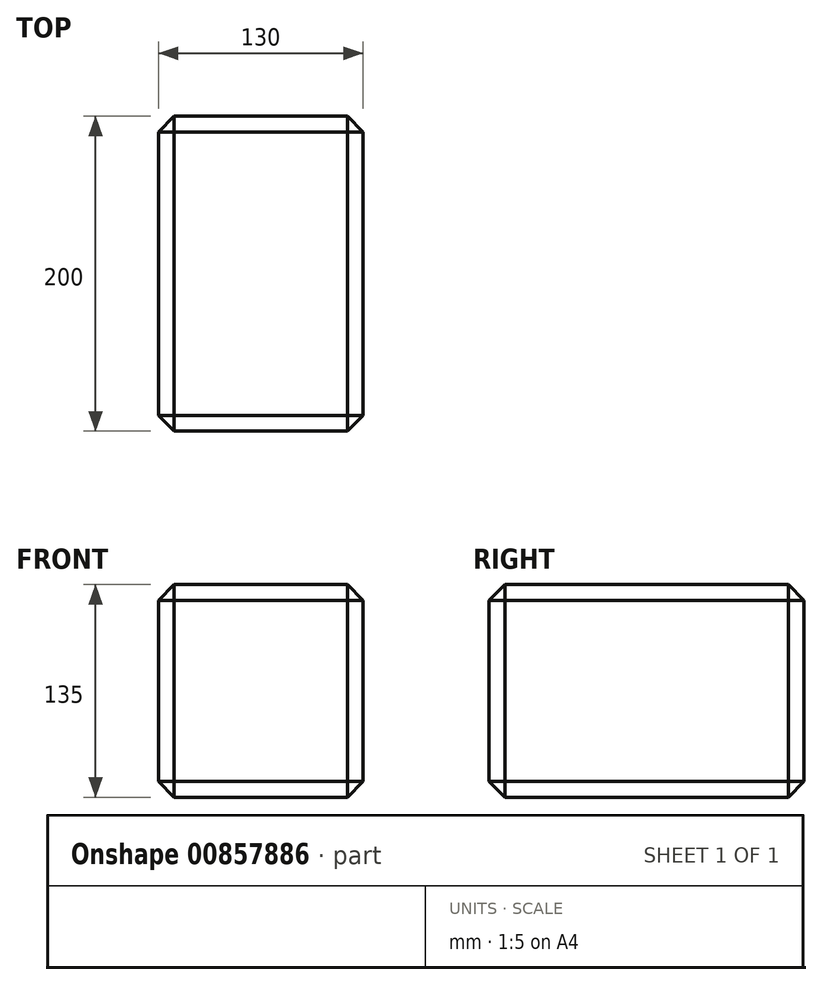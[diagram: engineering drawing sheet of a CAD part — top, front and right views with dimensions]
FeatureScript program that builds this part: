
annotation { "Feature Type Name" : "Feature", "Feature Type Description" : "" }
export const myFeature = defineFeature(function(context is Context, id is Id, definition is map)
    precondition{}
    {
        {
            var Q0;
            Q0=qCreatedBy(makeId("Top.planeOp"),FACE);
            var sketch = newSketch(context, id + "F0", { "sketchPlane" : qUnion([Q0])});
            skLineSegment(sketch, "E0.bottom", {"start": v(0, 0) * mm, "end": v(130, 0) * mm});
            skLineSegment(sketch, "E0.top", {"start": v(0, 200) * mm, "end": v(130, 200) * mm});
            skLineSegment(sketch, "E0.left", {"start": v(0, 0) * mm, "end": v(0, 200) * mm});
            skLineSegment(sketch, "E0.right", {"start": v(130, 0) * mm, "end": v(130, 200) * mm});
            skSolve(sketch);
        }
        {
            var Q0;
            Q0=qSketchRegion(id+"F0",true);
            extrude(context, id + "F1", {"entities" : qUnion([Q0]), "depth" : 135 * mm, "offsetDistance" : 25 * mm});
        }
        {
            var Q0;
            Q0=makeQuery(id+"F1.opExtrude","CAP_EDGE",EDGE,{"disambiguationData":[OSD([sQuery(id+"F0.wireOp",EDGE,"E0.bottom")])],"isStart":false});
            var Q1;
            Q1=makeQuery(id+"F1.opExtrude","CAP_EDGE",EDGE,{"disambiguationData":[OSD([sQuery(id+"F0.wireOp",EDGE,"E0.right")])],"isStart":false});
            var Q2;
            Q2=makeQuery(id+"F1.opExtrude","SWEPT_EDGE",EDGE,{"disambiguationData":[OSD([sQuery(id+"F0.wireOp",EDGE,"E0.bottom"),sQuery(id+"F0.wireOp",EDGE,"E0.right")])]});
            var Q3;
            Q3=makeQuery(id+"F1.opExtrude","SWEPT_EDGE",EDGE,{"disambiguationData":[OSD([sQuery(id+"F0.wireOp",EDGE,"E0.top"),sQuery(id+"F0.wireOp",EDGE,"E0.right")])]});
            var Q4;
            Q4=makeQuery(id+"F1.opExtrude","CAP_EDGE",EDGE,{"disambiguationData":[OSD([sQuery(id+"F0.wireOp",EDGE,"E0.top")])],"isStart":false});
            var Q5;
            Q5=makeQuery(id+"F1.opExtrude","CAP_EDGE",EDGE,{"disambiguationData":[OSD([sQuery(id+"F0.wireOp",EDGE,"E0.left")])],"isStart":false});
            var Q6;
            Q6=makeQuery(id+"F1.opExtrude","CAP_EDGE",EDGE,{"disambiguationData":[OSD([sQuery(id+"F0.wireOp",EDGE,"E0.right")])],"isStart":true});
            var Q7;
            Q7=makeQuery(id+"F1.opExtrude","CAP_EDGE",EDGE,{"disambiguationData":[OSD([sQuery(id+"F0.wireOp",EDGE,"E0.bottom")])],"isStart":true});
            var Q8;
            Q8=makeQuery(id+"F1.opExtrude","SWEPT_EDGE",EDGE,{"disambiguationData":[OSD([sQuery(id+"F0.wireOp",EDGE,"E0.bottom"),sQuery(id+"F0.wireOp",EDGE,"E0.left")])]});
            var Q9;
            Q9=makeQuery(id+"F1.opExtrude","SWEPT_EDGE",EDGE,{"disambiguationData":[OSD([sQuery(id+"F0.wireOp",EDGE,"E0.top"),sQuery(id+"F0.wireOp",EDGE,"E0.left")])]});
            var Q10;
            Q10=makeQuery(id+"F1.opExtrude","CAP_EDGE",EDGE,{"disambiguationData":[OSD([sQuery(id+"F0.wireOp",EDGE,"E0.left")])],"isStart":true});
            var Q11;
            Q11=makeQuery(id+"F1.opExtrude","CAP_EDGE",EDGE,{"disambiguationData":[OSD([sQuery(id+"F0.wireOp",EDGE,"E0.top")])],"isStart":true});
            chamfer(context, id + "F2", {"entities" : qUnion([Q0, Q1, Q2, Q3, Q4, Q5, Q6, Q7, Q8, Q9, Q10, Q11]), "width" : 10 * mm, "tangentPropagation" : true});
        }
    });
